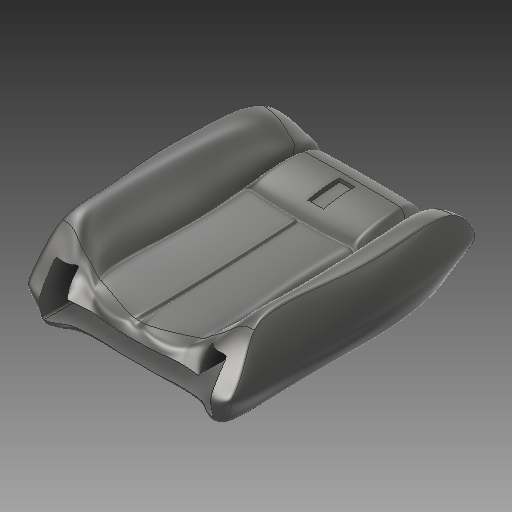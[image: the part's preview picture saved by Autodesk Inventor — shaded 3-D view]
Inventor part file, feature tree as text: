
AUTODESK INVENTOR PART (.ipt)
format: ipt  version: 2019 (Build 230136000, 136)  size: 2,471,424 bytes
history: native  units: in
note: dims shown in document units (in); Inventor stores cm internally (conversion verified against a paired STEP export)
features: sketch x12, plane x10, other x3, extrude x2, thicken_offset x1, hole x1, revolve x1, projected_geometry x1
ambient origin geometry x8: Origin, YZ Plane, XZ Plane, XY Plane, X Axis, Y Axis, Z Axis, Center Point
bodies: Solid7 (feature_tree)
feature tree (31):
  other  "Blocks"
  sketch  "Sketch3"  dims[d22=7.0866in d23=1.9685in]
  plane  "Work Plane2"
  sketch  "Sketch4"  dims[d24=0.9843in d25=3.1496in]
  plane  "Work Plane3"
  sketch  "Sketch5"  dims[d26=-6.2992in d27=-3.937in]
  plane  "Work Plane4"
  sketch  "Sketch6"  dims[d28=-11.811in d47=0.7874in]
  plane  "Work Plane5"
  sketch  "Sketch7"  dims[d48=27.5591in d49=0.0in]
  plane  "Work Plane6"
  sketch  "Sketch8"  dims[d53=0.5906in]
  plane  "Work Plane7"
  sketch  "Sketch9"  dims[d54=1.9685in]
  plane  "Work Plane8"
  sketch  "Sketch10"  dims[d55=4.7244in]
  other  "Form3"
  plane  "Work Plane11"
  thicken_offset  "Thicken2"
  extrude  "Extrusion7"  Depth=1.9685in
  extrude  "Extrusion3"  Depth=3.1496in
  plane  "Work Plane12"
  hole  "Hole1"  [1 undecoded]
  revolve  "Revolution1"  [1 undecoded]
  sketch  "Sketch13"  dims[d76=0.0344in d77=3.937in]
  plane  "Work Plane10"
  sketch  "Sketch17"  dims[d78=0.9843in d79=0.0in]
  other  "Block1"
  sketch  "Sketch19"  dims[d95=-31.4961in]
  sketch  "Sketch20"  dims[d96=6.6929in d97=3.3465in d98=0.5906in d99=0.2362in d100=0.1575in d101=0.0787in d102=90.0deg d103=1.9685in d104=0.8108in d105=3.3858in d107=6.6929in d108=8.6614in d109=0.1969in d110=2.3622in d115=0.022in d116=0.0197in d117=1.5748in d118=24.8031in d119=3.189in d120=0.3436in]
  projected_geometry  "Project Cut Edges1"
note: 2 required parameter values undecoded (feature->parameter linkage not recoverable at this tier; creation-order binding heuristic only, values carry confidence <= 0.55)